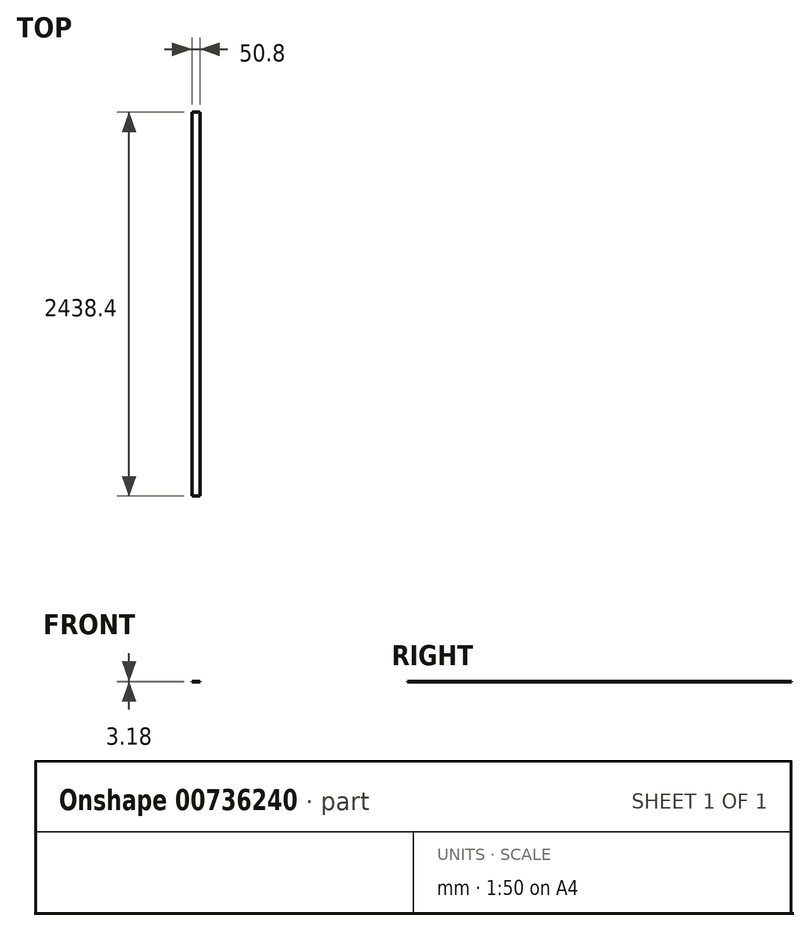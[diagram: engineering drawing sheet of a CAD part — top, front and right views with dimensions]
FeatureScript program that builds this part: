
annotation { "Feature Type Name" : "Feature", "Feature Type Description" : "" }
export const myFeature = defineFeature(function(context is Context, id is Id, definition is map)
    precondition{}
    {
        {
            var Q0;
            Q0=qCreatedBy(makeId("Front.planeOp"),FACE);
            var sketch = newSketch(context, id + "F0", { "sketchPlane" : qUnion([Q0])});
            skLineSegment(sketch, "E0.bottom", {"start": v(25.4, -1.59) * mm, "end": v(-25.4, -1.59) * mm});
            skLineSegment(sketch, "E0.top", {"start": v(25.4, 1.59) * mm, "end": v(-25.4, 1.59) * mm});
            skLineSegment(sketch, "E0.left", {"start": v(25.4, -1.59) * mm, "end": v(25.4, 1.59) * mm});
            skLineSegment(sketch, "E0.right", {"start": v(-25.4, -1.59) * mm, "end": v(-25.4, 1.59) * mm});
            skPoint(sketch, "E0.middle", {"position": v(0, 0) * mm});
            skSolve(sketch);
        }
        {
            var Q0;
            Q0 = qSketchRegion(id + "F0", true);
            extrude(context, id + "F1", {"entities" : qUnion([Q0]), "oppositeDirection" : true, "depth" : 2438.4 * mm, "offsetDistance" : 25.4 * mm});
        }
    });
